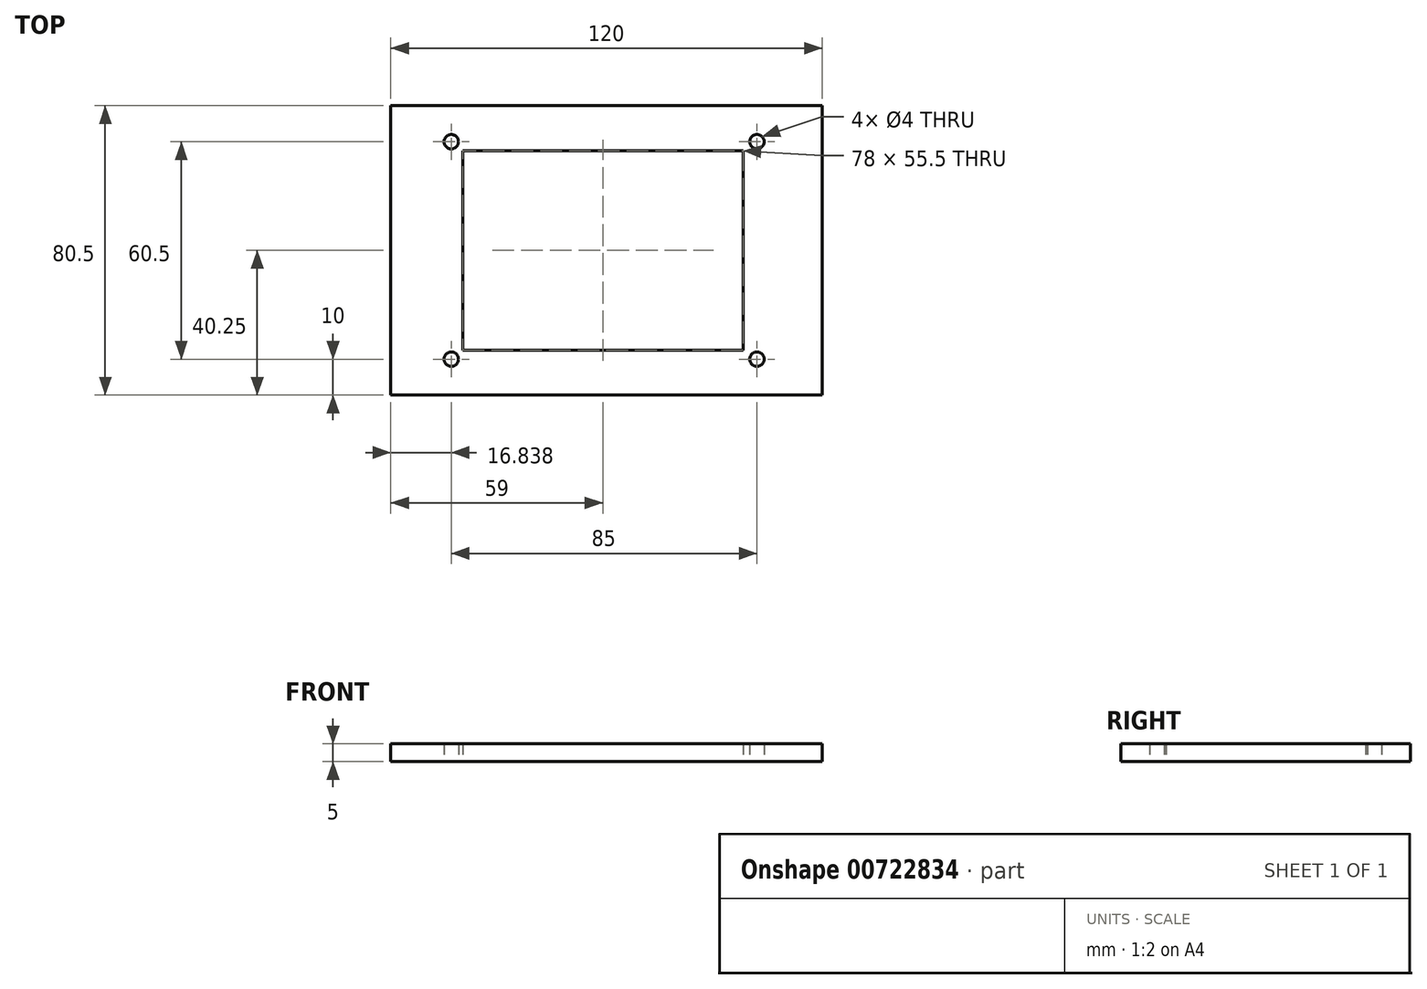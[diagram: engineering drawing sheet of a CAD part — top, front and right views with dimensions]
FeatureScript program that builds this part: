
annotation { "Feature Type Name" : "Feature", "Feature Type Description" : "" }
export const myFeature = defineFeature(function(context is Context, id is Id, definition is map)
    precondition{}
    {
        {
            var Q0;
            Q0=qCreatedBy(makeId("Top.planeOp"),FACE);
            var sketch = newSketch(context, id + "F0", { "sketchPlane" : qUnion([Q0])});
            skLineSegment(sketch, "E0.bottom", {"start": v(0, 0) * mm, "end": v(120, 0) * mm});
            skLineSegment(sketch, "E0.top", {"start": v(0, 80.5) * mm, "end": v(120, 80.5) * mm});
            skLineSegment(sketch, "E0.left", {"start": v(0, 0) * mm, "end": v(0, 80.5) * mm});
            skLineSegment(sketch, "E0.right", {"start": v(120, 0) * mm, "end": v(120, 80.5) * mm});
            skLineSegment(sketch, "E1.bottom", {"start": v(20, 12.5) * mm, "end": v(98, 12.5) * mm});
            skLineSegment(sketch, "E1.top", {"start": v(20, 68) * mm, "end": v(98, 68) * mm});
            skLineSegment(sketch, "E1.left", {"start": v(20, 12.5) * mm, "end": v(20, 68) * mm});
            skLineSegment(sketch, "E1.right", {"start": v(98, 12.5) * mm, "end": v(98, 68) * mm});
            skCircle(sketch, "E2", {"center": v(16.84, 10) * mm, "radius": 2 * mm});
            skCircle(sketch, "E3", {"center": v(16.84, 70.5) * mm, "radius": 2 * mm});
            skCircle(sketch, "E4", {"center": v(101.84, 70.5) * mm, "radius": 2 * mm});
            skCircle(sketch, "E5", {"center": v(101.84, 10) * mm, "radius": 2 * mm});
            skSolve(sketch);
        }
        {
            var Q0;
            Q0=makeQuery(id+"F0.imprint","IMPRINT",FACE,{"disambiguationData":[TD([[makeQuery(id+"F0.imprint","IMPRINT",EDGE,{"derivedFrom":sQuery(id+"F0.wireOp",EDGE,"E0.bottom")}),1.0]])]});
            extrude(context, id + "F1", {"entities" : qUnion([Q0]), "depth" : 5 * mm, "offsetDistance" : 25 * mm});
        }
    });
